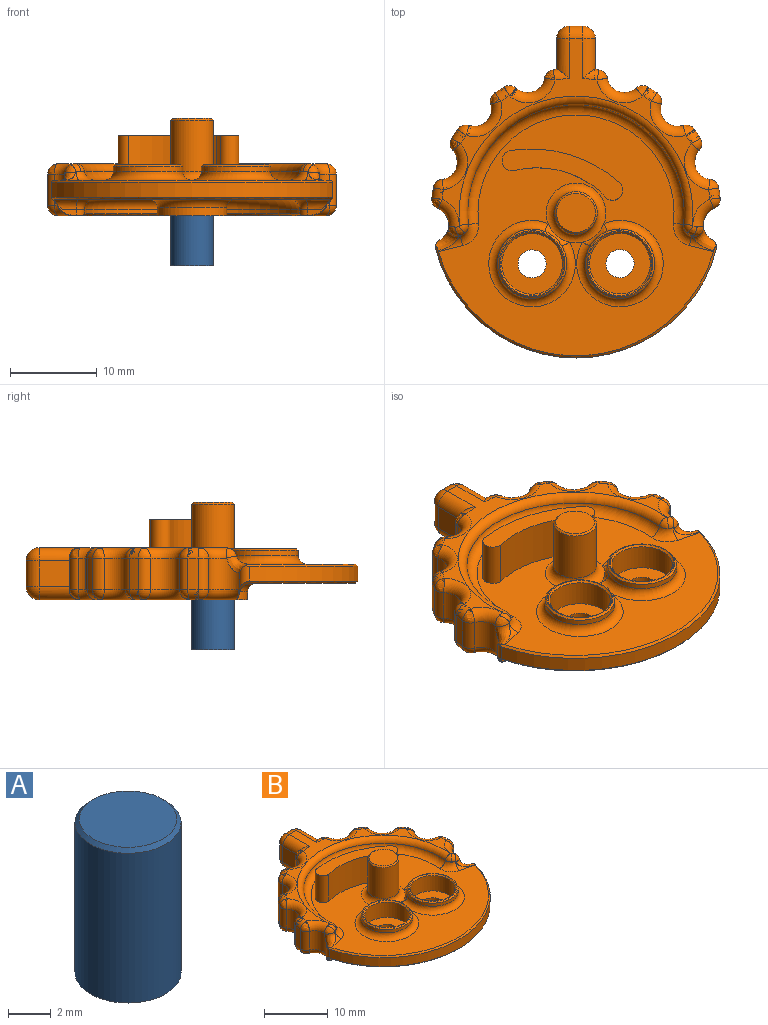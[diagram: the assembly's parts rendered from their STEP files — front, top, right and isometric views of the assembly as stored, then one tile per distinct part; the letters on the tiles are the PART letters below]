
ASSEMBLY  parts=2 mates=1
PART A: 4 faces, bbox 5x5x8.8 mm
  f0: cylinder r=2.48mm len=8.55mm, axis (0,0,-1), area 133mm2, adj f2,f3
  f1: plane 4.55x4.55mm, normal (0,0,1), area 16.3mm2, adj f3
  f2: plane 4.95x4.95mm, normal (0,0,-1), area 19.2mm2, adj f0
  f3: cone r=2.27mm half-angle=45deg, axis (0,0,-1), area 4.2mm2, adj f0,f1
PART B: 182 faces, bbox 33.4x38.4x11.5 mm
  f0: plane 31.77x27.83mm, normal (0,0,-1), area 495.7mm2, adj f1,f174,f175,f176,f177,f178,f179,f180
  f1: cylinder r=1.2mm len=3.09mm, axis (-0.97,0.24,0), area 4.3mm2, adj f0,f2,f174,f178
  f2: plane 2.2x1.21mm, normal (-0.24,-0.97,0), area 1mm2, adj f1,f3,f172,f173,f178
  f3: bspline ~1.85x1.33mm, area 0.3mm2, adj f2,f4,f171,f172
  f4: torus R=3.2mm, axis (0,0,1), area 8.4mm2, adj f3,f5,f169,f170
  f5: sphere r=1.2mm, area 1.8mm2, adj f4,f6,f168
  f6: cylinder r=1.2mm len=3.6mm, axis (0,0,1), area 5.5mm2, adj f5,f7,f167,f170
  f7: cylinder r=16.75mm len=3.6mm, axis (0,0,-1), area 4.3mm2, adj f6,f8,f166,f168
  f8: torus R=15.55mm, axis (0,0,1), area 2.2mm2, adj f7,f9,f165,f167
  f9: plane 30.94x21.71mm, normal (0,0,1), area 51mm2, adj f8,f10,f145,f146,f147,f148,f149,f150
  f10: cylinder r=1.5mm len=1.5mm, axis (1,0,0), area 3.5mm2, adj f9,f11,f143,f144
  f11: plane 3x1.5mm, normal (0,1,0), area 4.5mm2, adj f10,f12,f109,f142
  f12: cylinder r=1.5mm len=3mm, axis (0,0,1), area 7.1mm2, adj f11,f13,f108,f144
  f13: plane 3.5x3mm, normal (-1,0,0), area 10.5mm2, adj f12,f14,f107,f164
  f14: cylinder r=16.75mm len=3.6mm, axis (0,0,-1), area 1.4mm2, adj f13,f15,f106,f107,f163,f164
  f15: cylinder r=1.2mm len=3.6mm, axis (0,0,1), area 5.3mm2, adj f14,f16,f104,f105
  f16: cylinder r=2mm len=3.6mm, axis (0,0,-1), area 15.2mm2, adj f15,f17,f102,f162
  f17: torus R=3.2mm, axis (0,0,1), area 9.7mm2, adj f16,f18,f104,f169
  f18: sphere r=1.2mm, area 1mm2, adj f17,f19,f102
  f19: torus R=15.55mm, axis (0,0,1), area 2.3mm2, adj f18,f20,f101,f169
  f20: cylinder r=16.75mm len=3.6mm, axis (0,0,-1), area 4.5mm2, adj f19,f21,f102,f161
  f21: cylinder r=1.2mm len=3.6mm, axis (0,0,1), area 5.4mm2, adj f20,f22,f23,f101
  f22: sphere r=1.2mm, area 1mm2, adj f21,f160,f161
  f23: cylinder r=2mm len=3.6mm, axis (0,0,-1), area 15.5mm2, adj f21,f24,f99,f160
  f24: torus R=3.2mm, axis (0,0,1), area 9.9mm2, adj f23,f25,f101,f169
  f25: sphere r=1.2mm, area 1mm2, adj f24,f26,f99
  f26: torus R=15.55mm, axis (0,0,1), area 2.2mm2, adj f25,f27,f98,f169
  f27: cylinder r=16.75mm len=3.6mm, axis (0,0,-1), area 4.4mm2, adj f26,f28,f99,f159
  f28: cylinder r=1.2mm len=3.6mm, axis (0,0,1), area 5.5mm2, adj f27,f29,f30,f98
  f29: sphere r=1.2mm, area 1mm2, adj f28,f158,f159
  f30: cylinder r=2mm len=3.6mm, axis (0,0,-1), area 15.7mm2, adj f28,f31,f96,f158
  f31: torus R=3.2mm, axis (0,0,1), area 10mm2, adj f30,f32,f98,f169
  f32: sphere r=1.2mm, area 1mm2, adj f31,f33,f96
  f33: torus R=15.55mm, axis (0,0,1), area 2.2mm2, adj f32,f34,f95,f169
  f34: cylinder r=16.75mm len=3.6mm, axis (0,0,-1), area 4.3mm2, adj f33,f35,f96,f157
  f35: cylinder r=1.2mm len=3.6mm, axis (0,0,1), area 5.5mm2, adj f34,f36,f37,f95
  f36: sphere r=1.2mm, area 1mm2, adj f35,f156,f157
  f37: cylinder r=2mm len=3.6mm, axis (0,0,-1), area 13.7mm2, adj f35,f38,f47,f48,f94,f156,f178
  f38: torus R=3.2mm, axis (0,0,1), area 8.4mm2, adj f37,f39,f95,f169
  f39: bspline ~1.85x1.33mm, area 0.3mm2, adj f38,f40,f46,f47
  f40: plane 2.2x1.21mm, normal (0.24,-0.97,0), area 1mm2, adj f39,f41,f46,f177,f178
  f41: cylinder r=1.2mm len=1.29mm, axis (0,0,-1), area 1mm2, adj f40,f42,f43,f45,f176
  f42: cylinder r=12.53mm len=25.05mm, axis (0,0,-1), area 18.9mm2, adj f41,f43,f173,f175
  f43: cone r=12.78mm half-angle=45deg, axis (0,0,-1), area 15.3mm2, adj f41,f42,f44,f45,f169,f173
  f44: cone r=1.13mm half-angle=45deg, axis (0,0,1), area 0.1mm2, adj f43,f169,f172,f173
  f45: cone r=1.13mm half-angle=45deg, axis (0,0,1), area 0.1mm2, adj f41,f43,f46,f169
  f46: plane 0.39x0.16mm, normal (0.17,-0.69,-0.71), area 0mm2, adj f39,f40,f45,f169
  f47: plane 0.13x0.06mm, normal (-0.91,-0.41,0), area 0mm2, adj f37,f39,f178
  f48: cylinder r=1mm len=2.52mm, axis (0,0,1), area 2.5mm2, adj f37,f49,f93,f94,f178
  f49: cone r=16.5mm half-angle=45deg, axis (0,0,-1), area 15.6mm2, adj f48,f50,f89,f90,f91,f92,f93,f94
  f50: plane 31.77x27.83mm, normal (0,0,1), area 368.2mm2, adj f49,f51,f52,f55,f58,f60,f61,f62
  f51: torus R=11.33mm, axis (0,0,1), area 69.5mm2, adj f50,f52,f55,f154
  f52: torus R=2.4mm, axis (0,0,1), area 4.1mm2, adj f50,f51,f53,f89,f153
  f53: bspline ~1.46x1.08mm, area 1.3mm2, adj f52,f54,f152,f153
  f54: bspline ~1.38x1.21mm, area 1.6mm2, adj f53,f89,f90,f152
  f55: torus R=2.4mm, axis (0,0,1), area 4.1mm2, adj f50,f51,f56,f92,f155
  f56: bspline ~1.43x1.05mm, area 1mm2, adj f55,f57,f155,f156
  f57: bspline ~1.51x1.36mm, area 1.6mm2, adj f56,f92,f94,f156
  f58: cylinder r=1.18mm len=5.15mm, axis (0,0,-1), area 19.7mm2, adj f50,f59,f60,f63
  f59: plane 13.93x5.93mm, normal (0,0,1), area 31.3mm2, adj f58,f60,f61,f62,f63
  f60: cylinder r=15.35mm len=12.48mm, axis (0,0,-1), area 69.3mm2, adj f50,f58,f59,f61
  f61: cylinder r=1.19mm len=5.15mm, axis (0,0,-1), area 18.8mm2, adj f50,f59,f60,f62
  f62: cylinder r=11.09mm len=10.12mm, axis (0,0,-1), area 55.7mm2, adj f50,f59,f61,f63
  f63: cylinder r=10.37mm len=9.25mm, axis (0,0,-1), area 4.2mm2, adj f50,f58,f59,f62,f64,f68
  f64: plane 8x8mm, normal (0,0,-1), area 31.4mm2, adj f63,f65,f67,f68
  f65: cylinder r=2.45mm len=4.9mm, axis (0,0,-1), area 46.2mm2, adj f64,f66
  f66: plane 4.9x4.9mm, normal (0,0,-1), area 18.9mm2, adj f65
  f67: cylinder r=4mm len=8mm, axis (0,0,1), area 22.6mm2, adj f64,f181
  f68: cylinder r=1.18mm len=4.1mm, axis (0,0,-1), area 0.2mm2, adj f50,f63,f64
  f69: torus R=5mm, axis (0,0,1), area 38.5mm2, adj f50,f70,f71
  f70: bspline ~2.86x2.66mm, area 3mm2, adj f69,f71,f85
  f71: cylinder r=4mm len=8mm, axis (0,0,-1), area 15.1mm2, adj f69,f70,f72
  f72: cone r=3.8mm half-angle=45deg, axis (0,0,-1), area 6.9mm2, adj f71,f73
  f73: plane 7.6x7.6mm, normal (0,0,1), area 2.4mm2, adj f72,f74
  f74: cone r=3.7mm half-angle=45deg, axis (0,0,1), area 6.4mm2, adj f73,f75
  f75: cylinder r=3.5mm len=7mm, axis (0,0,-1), area 64.9mm2, adj f74,f76
  f76: plane 7x7mm, normal (0,0,1), area 30.2mm2, adj f75,f179
  f77: torus R=5mm, axis (0,0,1), area 38.5mm2, adj f50,f78,f79
  f78: bspline ~2.86x2.66mm, area 3mm2, adj f77,f79,f85
  f79: cylinder r=4mm len=8mm, axis (0,0,-1), area 15.1mm2, adj f77,f78,f80
  f80: cone r=4mm half-angle=45deg, axis (0,0,-1), area 6.9mm2, adj f79,f81
  f81: plane 7.6x7.6mm, normal (0,0,1), area 2.4mm2, adj f80,f82
  f82: cone r=3.7mm half-angle=45deg, axis (0,0,1), area 6.4mm2, adj f81,f83
  f83: cylinder r=3.5mm len=7mm, axis (0,0,-1), area 64.9mm2, adj f82,f84
  f84: plane 7x7mm, normal (0,0,1), area 30.2mm2, adj f83,f180
  f85: torus R=3.45mm, axis (0,0,1), area 27.8mm2, adj f50,f70,f78,f86
  f86: cylinder r=2.45mm len=5.95mm, axis (0,0,-1), area 91.6mm2, adj f85,f87
  f87: cone r=2.25mm half-angle=45deg, axis (0,0,-1), area 4.2mm2, adj f86,f88
  f88: plane 4.5x4.5mm, normal (0,0,1), area 15.9mm2, adj f87
  f89: cylinder r=1.2mm len=3.09mm, axis (0.97,-0.24,0), area 1.4mm2, adj f49,f50,f52,f54,f90
  f90: bspline ~2.96x2.86mm, area 5.1mm2, adj f49,f54,f89,f91,f170
  f91: cylinder r=1mm len=2.52mm, axis (0,0,1), area 2.5mm2, adj f49,f90,f93,f170,f178
  f92: cylinder r=1.2mm len=3.09mm, axis (0.97,0.24,0), area 1.4mm2, adj f49,f50,f55,f57,f94
  f93: cylinder r=16.75mm len=32.41mm, axis (0,0,-1), area 74.9mm2, adj f48,f49,f91,f178
  f94: bspline ~2.96x2.86mm, area 5.1mm2, adj f37,f48,f49,f57,f92
  f95: sphere r=1.2mm, area 2.7mm2, adj f33,f35,f38
  f96: cylinder r=1.2mm len=3.6mm, axis (0,0,1), area 5.5mm2, adj f30,f32,f34,f97
  f97: sphere r=1.2mm, area 2.7mm2, adj f96,f157,f158
  f98: sphere r=1.2mm, area 2.6mm2, adj f26,f28,f31
  f99: cylinder r=1.2mm len=3.6mm, axis (0,0,1), area 5.4mm2, adj f23,f25,f27,f100
  f100: sphere r=1.2mm, area 3.3mm2, adj f99,f159,f160
  f101: sphere r=1.2mm, area 2.6mm2, adj f19,f21,f24
  f102: cylinder r=1.2mm len=3.6mm, axis (0,0,1), area 5.3mm2, adj f16,f18,f20,f103
  f103: sphere r=1.2mm, area 3mm2, adj f102,f161,f162
  f104: sphere r=1.2mm, area 2.6mm2, adj f15,f17,f106
  f105: sphere r=1.2mm, area 1mm2, adj f15,f162,f163
  f106: torus R=15.55mm, axis (0,0,1), area 2mm2, adj f14,f104,f107,f169
  f107: cylinder r=1.5mm len=4.57mm, axis (0,-1,0), area 9mm2, adj f13,f14,f106,f108,f169
  f108: sphere r=1.5mm, area 2.2mm2, adj f12,f107,f109
  f109: cylinder r=1.5mm len=1.5mm, axis (-1,0,0), area 3.5mm2, adj f11,f108,f110,f169
  f110: sphere r=1.5mm, area 2.3mm2, adj f109,f111,f142
  f111: cylinder r=1.5mm len=4.57mm, axis (0,1,0), area 9mm2, adj f110,f112,f140,f141,f169
  f112: cylinder r=16.75mm len=3.6mm, axis (0,0,-1), area 1.4mm2, adj f111,f113,f140,f141,f145,f146
  f113: cylinder r=1.2mm len=3.6mm, axis (0,0,1), area 5.3mm2, adj f112,f114,f138,f139
  f114: cylinder r=2mm len=3.6mm, axis (0,0,-1), area 15.2mm2, adj f113,f115,f136,f147
  f115: cylinder r=1.2mm len=3.6mm, axis (0,0,1), area 5.3mm2, adj f114,f116,f134,f135
  f116: cylinder r=16.75mm len=3.6mm, axis (0,0,-1), area 4.5mm2, adj f115,f117,f132,f148
  f117: torus R=15.55mm, axis (0,0,1), area 2.3mm2, adj f116,f118,f135,f169
  f118: sphere r=1.2mm, area 1.3mm2, adj f117,f119,f132
  f119: torus R=3.2mm, axis (0,0,1), area 9.9mm2, adj f118,f120,f131,f169
  f120: sphere r=1.2mm, area 1.8mm2, adj f119,f121,f129
  f121: torus R=15.55mm, axis (0,0,1), area 2.2mm2, adj f120,f122,f128,f169
  f122: sphere r=1.2mm, area 1.5mm2, adj f121,f123,f126
  f123: torus R=3.2mm, axis (0,0,1), area 10mm2, adj f122,f124,f125,f169
  f124: sphere r=1.2mm, area 1.8mm2, adj f123,f166,f168
  f125: cylinder r=2mm len=3.6mm, axis (0,0,-1), area 15.7mm2, adj f123,f126,f151,f166
  f126: cylinder r=1.2mm len=3.6mm, axis (0,0,1), area 5.5mm2, adj f122,f125,f127,f128
  f127: sphere r=1.2mm, area 2.7mm2, adj f126,f150,f151
  f128: cylinder r=16.75mm len=3.6mm, axis (0,0,-1), area 4.4mm2, adj f121,f126,f129,f150
  f129: cylinder r=1.2mm len=3.6mm, axis (0,0,1), area 5.4mm2, adj f120,f128,f130,f131
  f130: sphere r=1.2mm, area 1.3mm2, adj f129,f149,f150
  f131: cylinder r=2mm len=3.6mm, axis (0,0,-1), area 15.5mm2, adj f119,f129,f132,f149
  f132: cylinder r=1.2mm len=3.6mm, axis (0,0,1), area 5.4mm2, adj f116,f118,f131,f133
  f133: sphere r=1.2mm, area 2.6mm2, adj f132,f148,f149
  f134: sphere r=1.2mm, area 1.5mm2, adj f115,f147,f148
  f135: sphere r=1.2mm, area 1.8mm2, adj f115,f117,f136
  f136: torus R=3.2mm, axis (0,0,1), area 9.7mm2, adj f114,f135,f137,f139,f169
  f137: sphere r=1.2mm, area 0.3mm2, adj f136,f141
  f138: sphere r=1.2mm, area 2.7mm2, adj f113,f146,f147
  f139: sphere r=1.2mm, area 0.6mm2, adj f113,f136,f141
  f140: plane 3.5x3mm, normal (1,0,0), area 10.5mm2, adj f111,f112,f142,f145
  f141: torus R=15.55mm, axis (0,0,1), area 2mm2, adj f111,f112,f137,f139,f169
  f142: cylinder r=1.5mm len=3mm, axis (0,0,-1), area 7.1mm2, adj f11,f110,f140,f143
  f143: sphere r=1.5mm, area 2.3mm2, adj f10,f142,f145
  f144: sphere r=1.5mm, area 4.8mm2, adj f10,f12,f164
  f145: cylinder r=1.5mm len=4.57mm, axis (0,-1,0), area 9mm2, adj f9,f112,f140,f143,f146
  f146: torus R=15.55mm, axis (0,0,1), area 2mm2, adj f9,f112,f138,f145
  f147: torus R=3.2mm, axis (0,0,1), area 9.7mm2, adj f9,f114,f134,f138
  f148: torus R=15.55mm, axis (0,0,1), area 2.3mm2, adj f9,f116,f133,f134
  f149: torus R=3.2mm, axis (0,0,1), area 9.9mm2, adj f9,f130,f131,f133
  f150: torus R=15.55mm, axis (0,0,1), area 2.2mm2, adj f9,f127,f128,f130
  f151: torus R=3.2mm, axis (0,0,1), area 10mm2, adj f9,f125,f127,f165
  f152: torus R=3.2mm, axis (0,0,1), area 5.9mm2, adj f9,f53,f54,f167,f170
  f153: torus R=0.22mm, axis (0,0,-1), area 1.1mm2, adj f9,f52,f53,f154
  f154: torus R=13.51mm, axis (0,0,1), area 62mm2, adj f9,f51,f153,f155
  f155: torus R=0.22mm, axis (0,0,-1), area 1.1mm2, adj f9,f55,f56,f154
  f156: torus R=3.2mm, axis (0,0,1), area 5.9mm2, adj f9,f36,f37,f56,f57
  f157: torus R=15.55mm, axis (0,0,1), area 2.2mm2, adj f9,f34,f36,f97
  f158: torus R=3.2mm, axis (0,0,1), area 10mm2, adj f9,f29,f30,f97
  f159: torus R=15.55mm, axis (0,0,1), area 2.2mm2, adj f9,f27,f29,f100
  f160: torus R=3.2mm, axis (0,0,1), area 9.9mm2, adj f9,f22,f23,f100
  f161: torus R=15.55mm, axis (0,0,1), area 2.3mm2, adj f9,f20,f22,f103
  f162: torus R=3.2mm, axis (0,0,1), area 9.7mm2, adj f9,f16,f103,f105
  f163: torus R=15.55mm, axis (0,0,1), area 2mm2, adj f9,f14,f105,f164
  f164: cylinder r=1.5mm len=4.57mm, axis (0,1,0), area 9mm2, adj f9,f13,f14,f144,f163
  f165: sphere r=1.2mm, area 1.9mm2, adj f8,f151,f166
  f166: cylinder r=1.2mm len=3.6mm, axis (0,0,1), area 5.5mm2, adj f7,f124,f125,f165
  f167: sphere r=1.2mm, area 2.7mm2, adj f6,f8,f152
  f168: torus R=15.55mm, axis (0,0,1), area 2.2mm2, adj f5,f7,f124,f169
  f169: plane 30.94x22.73mm, normal (0,0,-1), area 84.9mm2, adj f4,f17,f19,f24,f26,f31,f33,f38
  f170: cylinder r=2mm len=3.6mm, axis (0,0,-1), area 13.7mm2, adj f4,f6,f90,f91,f152,f171,f178
  f171: bspline ~0.13x0.06mm, area 0mm2, adj f3,f170,f178
  f172: plane 0.39x0.16mm, normal (-0.17,-0.69,-0.71), area 0mm2, adj f2,f3,f44,f169
  f173: cylinder r=1.2mm len=1.29mm, axis (0,0,-1), area 1mm2, adj f2,f42,f43,f44,f174
  f174: torus R=2.4mm, axis (0,0,1), area 4.4mm2, adj f0,f1,f173,f175
  f175: torus R=11.33mm, axis (0,0,1), area 76.4mm2, adj f0,f42,f174,f176
  f176: torus R=2.4mm, axis (0,0,1), area 4.4mm2, adj f0,f41,f175,f177
  f177: cylinder r=1.2mm len=3.09mm, axis (-0.97,-0.24,0), area 4.3mm2, adj f0,f40,f176,f178
  f178: cone r=16.75mm half-angle=45deg, axis (0,0,1), area 16.7mm2, adj f0,f1,f2,f37,f40,f47,f48,f91
  f179: cylinder r=1.62mm len=3.25mm, axis (0,0,-1), area 8.7mm2, adj f0,f76
  f180: cylinder r=1.62mm len=3.25mm, axis (0,0,-1), area 8.7mm2, adj f0,f84
  f181: torus R=5mm, axis (0,0,1), area 43.1mm2, adj f0,f67
PLACE A t=(7.39,-7.94,-8.17)mm
PLACE B t=(7.39,-7.94,0.61)mm
MATE slider A.f0 <-> B.f65  axis (0,0,-1) through (7.39,-7.94,-8.17)mm
